# Revit family: Gira_100400
name_source: partatom
category: Elektroinstallationen
revit_build: Autodesk Revit 2017 (Build: 20160225_1515(x64)
units: mm (PartAtom-declared; Revit-internal decimal feet)

## family parameters
Basisbauteil = Fläche
Beim Laden mit Abzugskörper schneiden = Nein
Bemaßung runder Anschluss = Durchmesser verwenden
Beschriftungsausrichtung beibehalten = Nein
Gemeinsam genutzt = Nein
Raumberechnungspunkt = Nein
Teiletyp = Normal

## types (1)
- Schaltaktor 4f 16 A Hand KNX REG
    Andere Bussysteme = ohne
    Anzahl der binären Eingänge = 4
    BIM = https://media.stage.bim.site 8f.rfa
    BIMSITE_PRODUCT_ID = 4afbc9e1e2d5739ea50aa643bc9d019e7483cc82
    Beschreibung = KNX Schaltaktor 4fach 16 A mit Handbetätigung  REG plus REG-Schaltaktoren mit integrierter Busankopplung. Zum Schalten von unabhängig ansteuerbaren Lastgruppen. Mit Handschalter zur Umschaltung des Relais (Ein Aus) parallel bzw. ohne KNX Betrieb. Anschluss mehrphasig. Keine zusätzliche Spannungsversorgung erforderlich.  Merkmale:  Handbetätigung der Relais unabhängig vom Bus bzw. der Schaltstellungsanzeige.  Schließer- oder Öffnerbetrieb.  Zentrale Schaltfunktion.  Sammelrückmeldung zur Reduzierung der Buslast.  Aktive oder passive (Objekt auslesbar) zyklische Rückmeldefunktion.  Rückmeldungen lassen sich nach Busspannungswiederkehr verzögern.  Logische Verknüpfungsfunktion für jeden Ausgang.  Sperrfunktion für jeden Kanal parametrierbar. Alternativ Zwangsstellungsfunktion für jeden Ausgang.  Zeitfunktionen (Ein- bzw. Ausschaltverzögerung, Treppenlichtfunktion - auch mit Vorwarnfunktion).  Einbeziehung in Lichtszenen möglich, max. acht interne Szenen je Kanal sind parametrierbar.  Speicherfunktion für Lichtszenen.  Betriebsstundenzähler als Vorwärts- Rückwärtszähler mit Grenzwertfunktion (Grenzwert über Bus veränderbar) für jeden Ausgang aktivierbar.  Eingangsüberwachung auf zyklische Aktualisierung mit Sicherheitsstellung.  Reaktionen bei Busspannungsausfall und -wiederkehr und nach einem ETS-Programmiervorgang für jeden Kanal einstellbar.  Unabhängiges Schalten der vier Ausgänge.  Hinweise :  Montage auf DIN-Hutschiene.  VDE-Zulassung gemäß EN 60669-1, EN 60669-2-1.
    Breite in Teilungseinheiten = 4
    Bussystem Funkbus = Nein
    Bussystem KNX = Ja
    Bussystem KNX-Funk = Nein
    Bussystem LON = Nein
    Bussystem Powernet = Nein
    Datenblatt = https://media.stage.bim.site
    Datenblatt 1 = https://media.stage.bim.site
    GTIN = 4010337042174
    Geeignet für C-Last = Nein
    HAN = 100400
    HeinzeBIM = https://www.heinze.de
    Hersteller = Gira
    Kosten = 0 $
    Max. Anzahl der Schaltausgänge = 4
    Mit Busankopplung = Nein
    Mit LED-Anzeige = Nein
    Montageart = REG
    Produktseite = https://media.stage.bim.site
    Schutzart (IP) = IP20
    Typname = Schaltaktor 4f 16 A Hand KNX REG
    URL = https://www.gira.de
    Vor Ort-/Handbedienung = Ja
    Vorgabe-Ansicht = 1219 mm

## geometry (parser evidence)
native form markers: Sweep x2
no freeform markers — native parametric forms only
